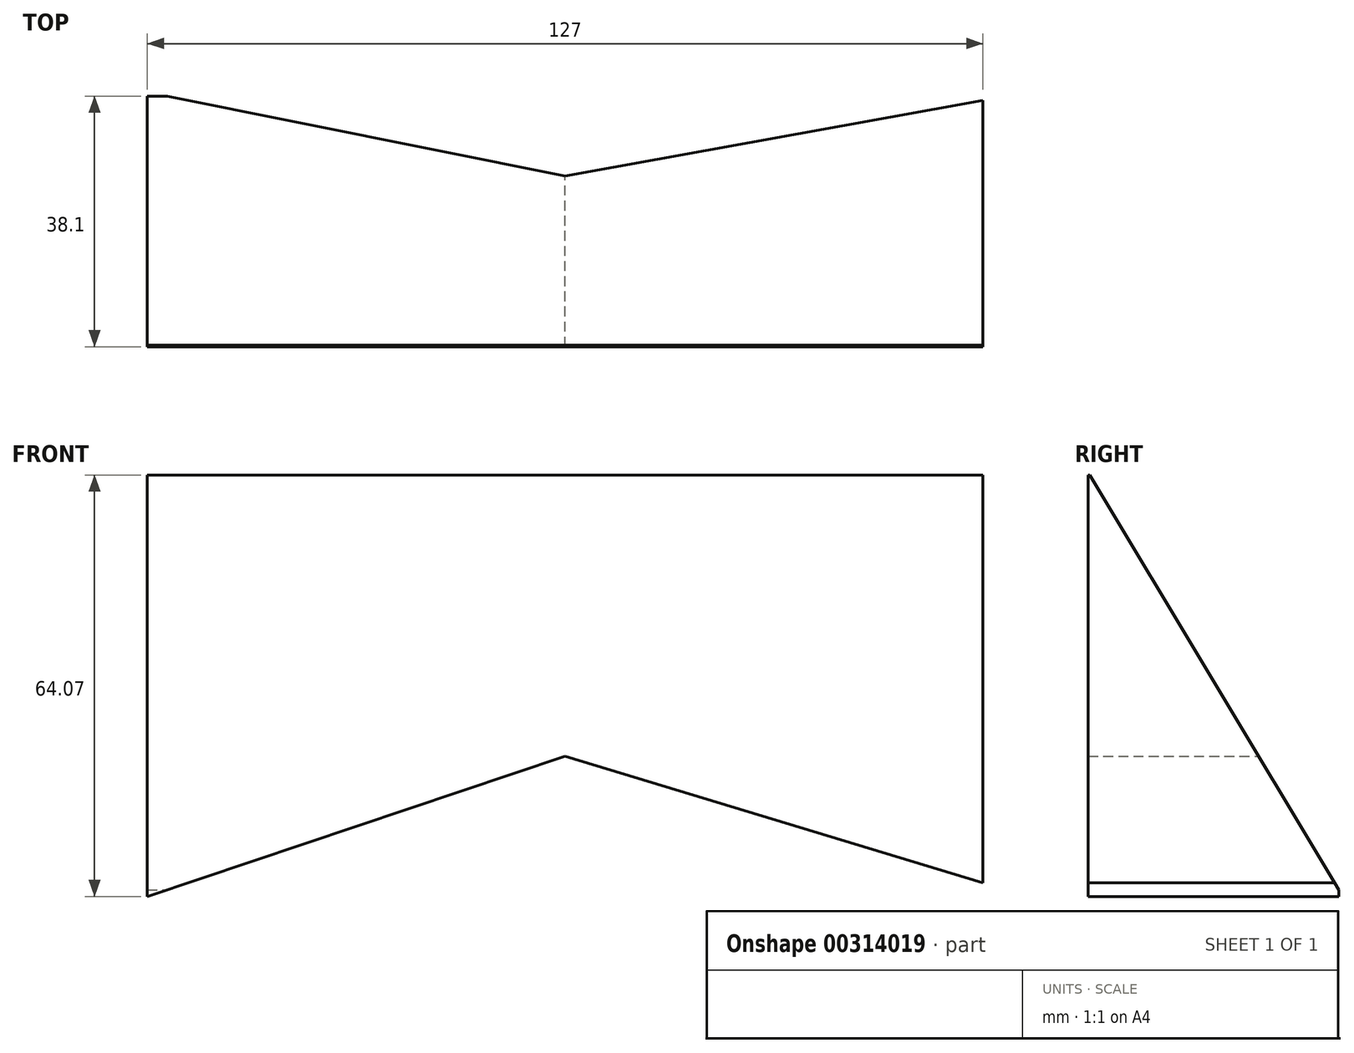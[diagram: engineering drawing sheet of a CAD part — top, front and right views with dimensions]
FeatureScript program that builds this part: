
annotation { "Feature Type Name" : "Feature", "Feature Type Description" : "" }
export const myFeature = defineFeature(function(context is Context, id is Id, definition is map)
    precondition{}
    {
        {
            var Q0;
            Q0=qCreatedBy(makeId("Front.planeOp"),FACE);
            var sketch = newSketch(context, id + "F0", { "sketchPlane" : qUnion([Q0])});
            skLineSegment(sketch, "E0", {"start": v(0, 42.8) * mm, "end": v(63.5, 42.8) * mm});
            skLineSegment(sketch, "E1", {"start": v(-63.5, 42.8) * mm, "end": v(-63.5, -21.28) * mm});
            skLineSegment(sketch, "E2", {"start": v(63.5, 42.8) * mm, "end": v(63.5, -19.2) * mm});
            skPoint(sketch, "E3.start.orphan", {"position": v(3.53, 0) * mm});
            skPoint(sketch, "E4.end.orphan", {"position": v(0, 0) * mm});
            skPoint(sketch, "E4.start.orphan", {"position": v(0, 42.8) * mm});
            skLineSegment(sketch, "E5", {"start": v(-63.5, 42.8) * mm, "end": v(0, 42.8) * mm});
            skLineSegment(sketch, "E6", {"start": v(-63.5, -21.28) * mm, "end": v(0, 0) * mm});
            skLineSegment(sketch, "E7", {"start": v(0, 0) * mm, "end": v(63.5, -19.2) * mm});
            skSolve(sketch);
        }
        {
            var Q0;
            Q0 = qSketchRegion(id + "F0", true);
            extrude(context, id + "F1", {"entities" : qUnion([Q0]), "depth" : 38.1 * mm});
        }
        {
            var Q0;
            Q0=qCreatedBy(makeId("Right.planeOp"),FACE);
            var sketch = newSketch(context, id + "F2", { "sketchPlane" : qUnion([Q0])});
            skLineSegment(sketch, "E8", {"start": v(0, 43.28) * mm, "end": v(-38.18, 43.28) * mm});
            skLineSegment(sketch, "E9", {"start": v(0, 43.28) * mm, "end": v(0, -20.26) * mm});
            skLineSegment(sketch, "E10", {"start": v(-38.18, 43.28) * mm, "end": v(0, -20.26) * mm});
            skSolve(sketch);
        }
        {
            var Q0;
            Q0 = qSketchRegion(id + "F2", true);
            extrude(context, id + "F3", {"entities" : qUnion([Q0]), "operationType" : NewBodyOperationType.REMOVE, "oppositeDirection" : true, "depth" : 106.17 * mm});
        }
        {
            var Q0;
            Q0 = qSketchRegion(id + "F2", true);
            extrude(context, id + "F4", {"entities" : qUnion([Q0]), "operationType" : NewBodyOperationType.REMOVE, "depth" : 85.6 * mm});
        }
    });
